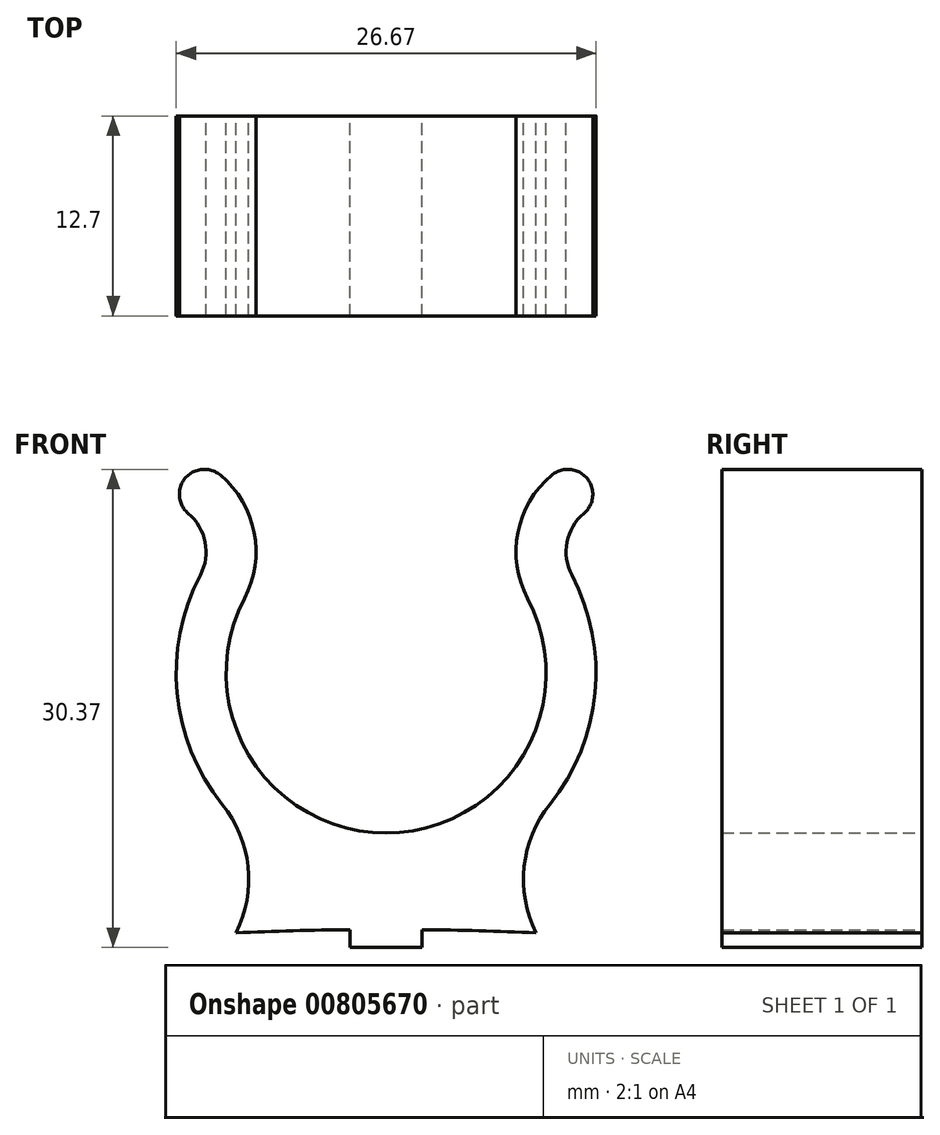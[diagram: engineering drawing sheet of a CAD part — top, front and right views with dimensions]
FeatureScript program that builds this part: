
annotation { "Feature Type Name" : "Feature", "Feature Type Description" : "" }
export const myFeature = defineFeature(function(context is Context, id is Id, definition is map)
    precondition{}
    {
        {
            var Q0;
            Q0=qCreatedBy(makeId("Front.planeOp"),FACE);
            var sketch = newSketch(context, id + "F0", { "sketchPlane" : qUnion([Q0])});
            skArc(sketch, "E0", {"start": v(-8.99, 4.74) * mm, "mid": v(0, -10.16) * mm, "end": v(8.99, 4.74) * mm});
            skArc(sketch, "E1", {"start": v(-11.8, 6.22) * mm, "mid": v(-13.27, -1.27) * mm, "end": v(-10.4, -8.34) * mm});
            skArc(sketch, "E2", {"start": v(10.52, 12.56) * mm, "mid": v(8.37, 8.92) * mm, "end": v(8.99, 4.74) * mm});
            skArc(sketch, "E3.MirrorC", {"start": v(-10.52, 12.56) * mm, "mid": v(-8.37, 8.92) * mm, "end": v(-8.99, 4.74) * mm});
            skArc(sketch, "E4", {"start": v(12.56, 10.13) * mm, "mid": v(11.49, 8.31) * mm, "end": v(11.8, 6.22) * mm});
            skArc(sketch, "E5.MirrorC", {"start": v(-12.56, 10.13) * mm, "mid": v(-11.49, 8.31) * mm, "end": v(-11.8, 6.22) * mm});
            skArc(sketch, "E6", {"start": v(12.56, 10.13) * mm, "mid": v(12.76, 12.37) * mm, "end": v(10.52, 12.56) * mm});
            skArc(sketch, "E7.MirrorCS", {"start": v(-12.56, 10.13) * mm, "mid": v(-12.76, 12.37) * mm, "end": v(-10.52, 12.56) * mm});
            skLineSegment(sketch, "E8", {"start": v(11.54, 11.35) * mm, "end": v(14.6, 7.7) * mm, "construction": true});
            skArc(sketch, "E9", {"start": v(-9.53, -16.51) * mm, "mid": v(-8.77, -12.3) * mm, "end": v(-10.4, -8.34) * mm});
            skArc(sketch, "E10.MirrorCS", {"start": v(9.53, -16.51) * mm, "mid": v(8.77, -12.3) * mm, "end": v(10.4, -8.34) * mm});
            skLineSegment(sketch, "E11.top", {"start": v(-2.29, -17.44) * mm, "end": v(2.29, -17.44) * mm});
            skLineSegment(sketch, "E11.left", {"start": v(-2.29, -16.3) * mm, "end": v(-2.29, -17.44) * mm});
            skLineSegment(sketch, "E11.right", {"start": v(2.29, -16.3) * mm, "end": v(2.29, -17.44) * mm});
            skArc(sketch, "E12.trimOffspring", {"start": v(10.4, -8.34) * mm, "mid": v(13.27, -1.27) * mm, "end": v(11.8, 6.22) * mm});
            skArc(sketch, "E13", {"start": v(9.53, -16.5) * mm, "mid": v(5.9, -16.38) * mm, "end": v(2.29, -16.3) * mm});
            skArc(sketch, "E14.trimOffspring", {"start": v(-2.29, -16.3) * mm, "mid": v(-5.9, -16.38) * mm, "end": v(-9.52, -16.5) * mm});
            skSolve(sketch);
        }
        {
            var Q0;
            Q0=makeQuery(id+"F0.imprint","IMPRINT",FACE,{"disambiguationData":[TD([[makeQuery(id+"F0.imprint","IMPRINT",EDGE,{"derivedFrom":sQuery(id+"F0.wireOp",EDGE,"E0")}),-1.0]])]});
            extrude(context, id + "F1", {"entities" : qUnion([Q0]), "depth" : 12.7 * mm, "offsetDistance" : 25.4 * mm});
        }
    });
